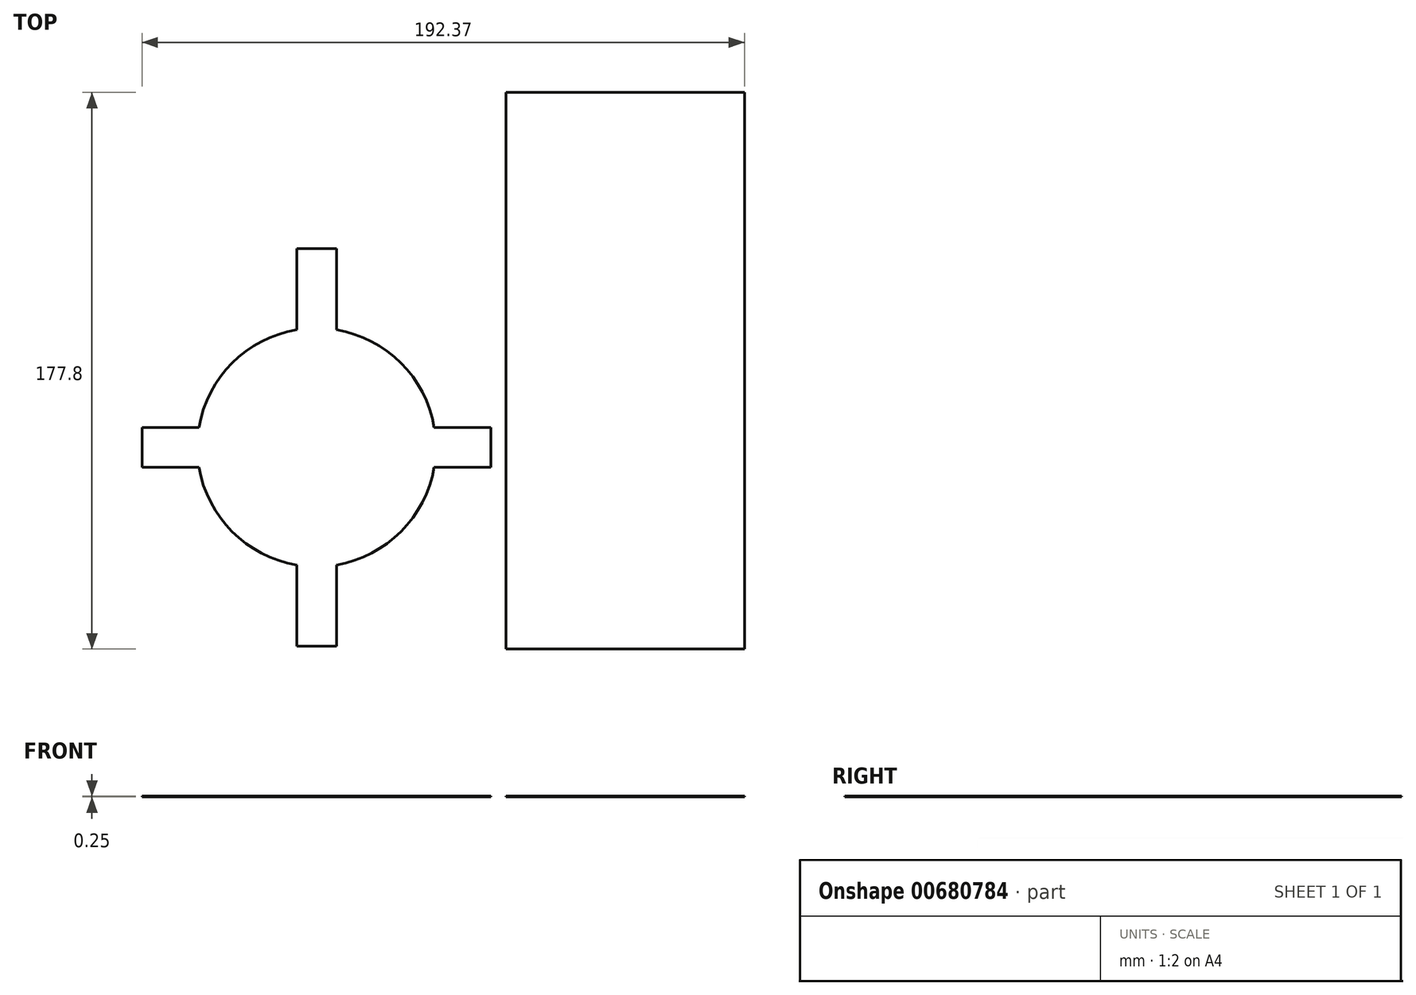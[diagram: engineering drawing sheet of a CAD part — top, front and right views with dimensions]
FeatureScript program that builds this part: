
annotation { "Feature Type Name" : "Feature", "Feature Type Description" : "" }
export const myFeature = defineFeature(function(context is Context, id is Id, definition is map)
    precondition{}
    {
        {
            var Q0;
            Q0=qCreatedBy(makeId("Top.planeOp"),FACE);
            var sketch = newSketch(context, id + "F0", { "sketchPlane" : qUnion([Q0])});
            skCircle(sketch, "E0", {"center": v(-39.42, 10.01) * mm, "radius": 38.1 * mm});
            skLineSegment(sketch, "E1.bottom", {"start": v(16.3, 3.66) * mm, "end": v(-95.14, 3.66) * mm});
            skLineSegment(sketch, "E1.top", {"start": v(16.3, 16.36) * mm, "end": v(-95.14, 16.36) * mm});
            skLineSegment(sketch, "E1.left", {"start": v(16.3, 3.66) * mm, "end": v(16.3, 16.36) * mm});
            skLineSegment(sketch, "E1.right", {"start": v(-95.14, 3.66) * mm, "end": v(-95.14, 16.36) * mm});
            skLineSegment(sketch, "E2.bottom", {"start": v(-45.77, 73.51) * mm, "end": v(-33.07, 73.51) * mm});
            skLineSegment(sketch, "E2.top", {"start": v(-45.77, -53.49) * mm, "end": v(-33.07, -53.49) * mm});
            skLineSegment(sketch, "E2.left", {"start": v(-45.77, 73.51) * mm, "end": v(-45.77, -53.49) * mm});
            skLineSegment(sketch, "E2.right", {"start": v(-33.07, 73.51) * mm, "end": v(-33.07, -53.49) * mm});
            skLineSegment(sketch, "E3.bottom", {"start": v(97.23, -54.44) * mm, "end": v(21.03, -54.44) * mm});
            skLineSegment(sketch, "E3.top", {"start": v(97.23, 123.36) * mm, "end": v(21.03, 123.36) * mm});
            skLineSegment(sketch, "E3.left", {"start": v(97.23, -54.44) * mm, "end": v(97.23, 123.36) * mm});
            skLineSegment(sketch, "E3.right", {"start": v(21.03, -54.44) * mm, "end": v(21.03, 123.36) * mm});
            skPoint(sketch, "E3.middle", {"position": v(59.13, 34.46) * mm});
            skSolve(sketch);
        }
        {
            var Q0;
            Q0 = qSketchRegion(id + "F0", true);
            var Q1;
            {var subQ0=sQuery(id+"F0.wireOp",EDGE,"E2.right");var subQ1=sQuery(id+"F0.wireOp",EDGE,"E1.bottom");var subQ2=makeQuery(id+"F0.imprint","INTERSECT",VERTEX,{"derivedFrom":[subQ1,subQ0]});Q1=makeQuery(id+"F0.imprint","IMPRINT",FACE,{"disambiguationData":[TD([[makeQuery(id+"F0.imprint","IMPRINT",EDGE,{"disambiguationData":[TD([[subQ2,-1.0]])],"derivedFrom":subQ1}),-1.0]])]});}
            extrude(context, id + "F1", {"entities" : qUnion([Q0, Q1]), "depth" : 0.25 * mm, "offsetDistance" : 25.4 * mm});
        }
    });
